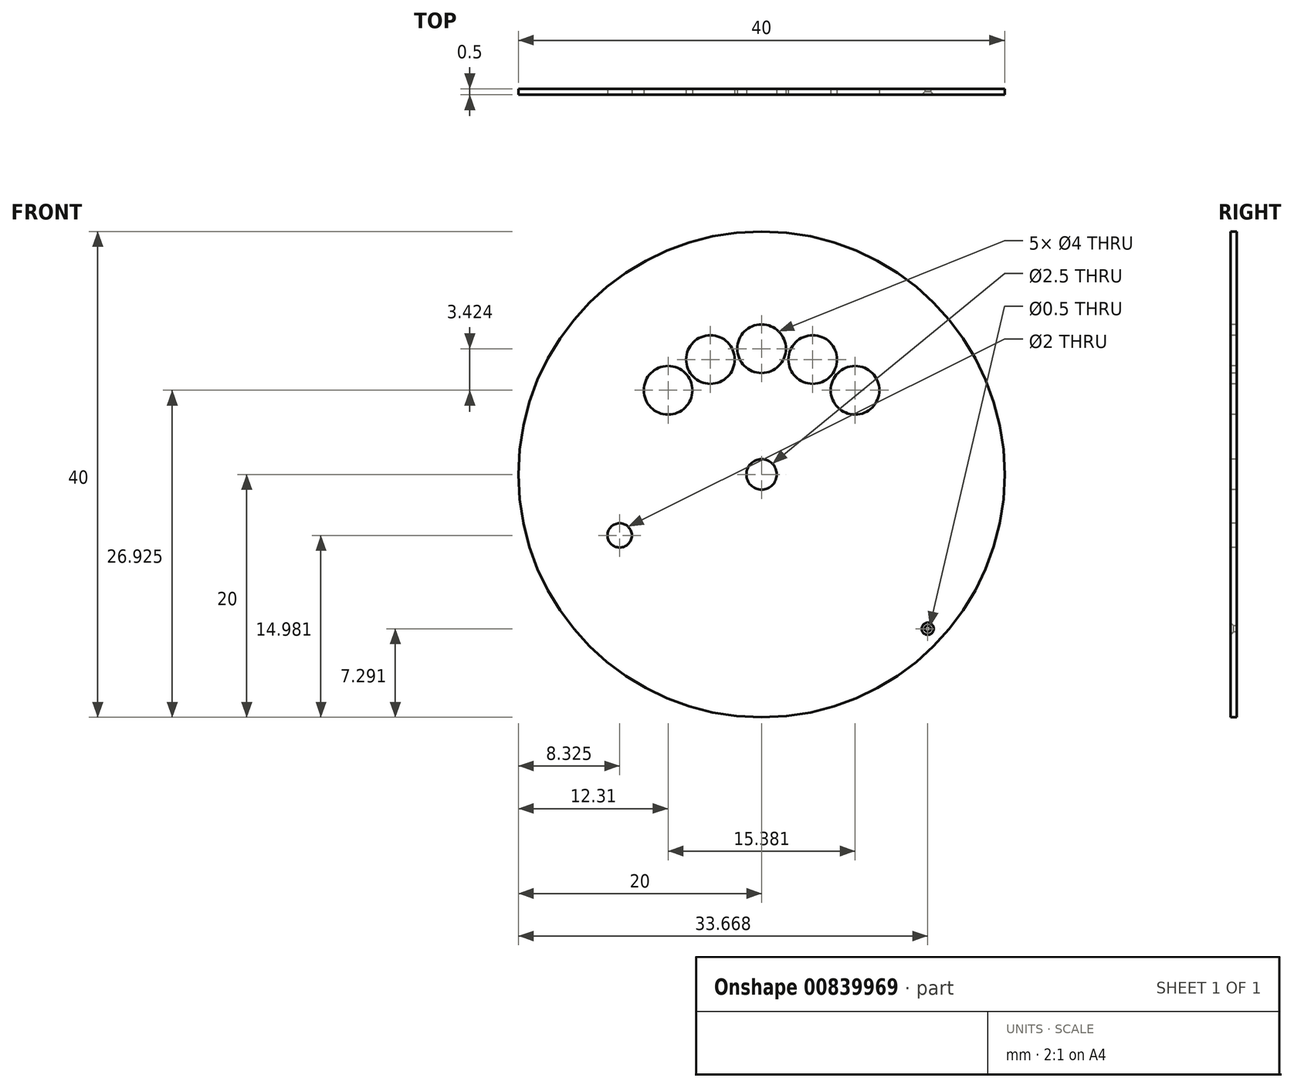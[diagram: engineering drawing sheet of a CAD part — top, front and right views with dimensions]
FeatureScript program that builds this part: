
annotation { "Feature Type Name" : "Feature", "Feature Type Description" : "" }
export const myFeature = defineFeature(function(context is Context, id is Id, definition is map)
    precondition{}
    {
        {
            var Q0;
            Q0=qCreatedBy(makeId("Front.planeOp"),FACE);
            var sketch = newSketch(context, id + "F0", { "sketchPlane" : qUnion([Q0])});
            skCircle(sketch, "E0", {"center": v(0, 0) * mm, "radius": 20 * mm});
            skSolve(sketch);
        }
        {
            var Q0;
            Q0 = qSketchRegion(id + "F0", true);
            extrude(context, id + "F1", {"entities" : qUnion([Q0]), "depth" : .5 * mm, "offsetDistance" : 25.4 * mm});
        }
        {
            var Q0;
            Q0=makeQuery(id+"F1.opExtrude","CAP_FACE",FACE,{"disambiguationData":[OSD([sQuery(id+"F0.wireOp",EDGE,"E0")])],"isStart":false});
            var sketch = newSketch(context, id + "F2", { "sketchPlane" : qUnion([Q0])});
            skPoint(sketch, "E1", {"position": v(0, 0) * mm});
            skSolve(sketch);
        }
        {
            var Q0;
            Q0=sQuery(id+"F2.wireOp",VERTEX,"E1");
            var Q1;
            Q1=makeQuery(id+"F1.opExtrude","SWEPT_BODY",BODY,{"disambiguationData":[OSD([sQuery(id+"F0.wireOp",EDGE,"E0")])]});
            hole(context, id + "F3", {"style" : HoleStyle.SIMPLE, "endStyle" : HoleEndStyle.THROUGH, "holeDiameter" : 2.5 * mm, "majorDiameter" : 6.35 * mm, "isTappedThrough" : true, "tappedDepth" : 12.7 * mm, "tapClearance" : 3, "locations" : qUnion([Q0]), "scope" : qUnion([Q1])});
        }
        {
            var Q0;
            Q0=makeQuery(id+"F1.opExtrude","CAP_FACE",FACE,{"disambiguationData":[OSD([sQuery(id+"F0.wireOp",EDGE,"E0")])],"isStart":false});
            var sketch = newSketch(context, id + "F4", { "sketchPlane" : qUnion([Q0])});
            skLineSegment(sketch, "E2", {"start": v(0, 0) * mm, "end": v(-22.97, 13.26) * mm, "construction": true});
            skLineSegment(sketch, "E3", {"start": v(-22.97, 13.26) * mm, "end": v(0, 0) * mm, "construction": true});
            skLineSegment(sketch, "E4", {"start": v(22.81, 13.17) * mm, "end": v(0, 0) * mm, "construction": true});
            skCircle(sketch, "E5", {"center": v(0, 0) * mm, "radius": 12.5 * mm, "construction": true});
            skCircle(sketch, "E6", {"center": v(-7.7, 6.92) * mm, "radius": 2.15 * mm, "construction": true});
            skCircle(sketch, "E7", {"center": v(-4.2, 9.45) * mm, "radius": 2.15 * mm, "construction": true});
            skCircle(sketch, "E8", {"center": v(0, 10.35) * mm, "radius": 2.15 * mm, "construction": true});
            skCircle(sketch, "E9", {"center": v(4.2, 9.45) * mm, "radius": 2.15 * mm, "construction": true});
            skCircle(sketch, "E10", {"center": v(7.7, 6.92) * mm, "radius": 2.15 * mm, "construction": true});
            skCircle(sketch, "E11", {"center": v(-7.7, 6.92) * mm, "radius": 2 * mm});
            skCircle(sketch, "E12", {"center": v(-4.2, 9.45) * mm, "radius": 2 * mm});
            skCircle(sketch, "E13", {"center": v(0, 10.35) * mm, "radius": 2 * mm});
            skCircle(sketch, "E14", {"center": v(4.2, 9.45) * mm, "radius": 2 * mm});
            skCircle(sketch, "E15", {"center": v(7.7, 6.92) * mm, "radius": 2 * mm});
            skSolve(sketch);
        }
        {
            var Q0;
            Q0=makeQuery(id+"F4.imprint","IMPRINT",FACE,{"disambiguationData":[TD([[makeQuery(id+"F4.imprint","IMPRINT",EDGE,{"derivedFrom":sQuery(id+"F4.wireOp",EDGE,"E11")}),1.0]])]});
            var Q1;
            Q1=makeQuery(id+"F4.imprint","IMPRINT",FACE,{"disambiguationData":[TD([[makeQuery(id+"F4.imprint","IMPRINT",EDGE,{"derivedFrom":sQuery(id+"F4.wireOp",EDGE,"E12")}),1.0]])]});
            var Q2;
            Q2=makeQuery(id+"F4.imprint","IMPRINT",FACE,{"disambiguationData":[TD([[makeQuery(id+"F4.imprint","IMPRINT",EDGE,{"derivedFrom":sQuery(id+"F4.wireOp",EDGE,"E13")}),1.0]])]});
            var Q3;
            Q3=makeQuery(id+"F4.imprint","IMPRINT",FACE,{"disambiguationData":[TD([[makeQuery(id+"F4.imprint","IMPRINT",EDGE,{"derivedFrom":sQuery(id+"F4.wireOp",EDGE,"E14")}),1.0]])]});
            var Q4;
            Q4=makeQuery(id+"F4.imprint","IMPRINT",FACE,{"disambiguationData":[TD([[makeQuery(id+"F4.imprint","IMPRINT",EDGE,{"derivedFrom":sQuery(id+"F4.wireOp",EDGE,"E15")}),1.0]])]});
            extrude(context, id + "F5", {"entities" : qUnion([Q0, Q1, Q2, Q3, Q4]), "operationType" : NewBodyOperationType.REMOVE, "oppositeDirection" : true, "depth" : 25.4 * mm, "offsetDistance" : 25.4 * mm});
        }
        {
            var Q0;
            Q0=makeQuery(id+"F1.opExtrude","CAP_FACE",FACE,{"disambiguationData":[OSD([sQuery(id+"F0.wireOp",EDGE,"E0")])],"isStart":false});
            var sketch = newSketch(context, id + "F6", { "sketchPlane" : qUnion([Q0])});
            skPoint(sketch, "E16", {"position": v(13.67, -12.7) * mm});
            skSolve(sketch);
        }
        {
            var Q0;
            Q0=sQuery(id+"F6.wireOp",VERTEX,"E16");
            var Q1;
            Q1=makeQuery(id+"F1.opExtrude","SWEPT_BODY",BODY,{"disambiguationData":[OSD([sQuery(id+"F0.wireOp",EDGE,"E0")])]});
            hole(context, id + "F7", {"style" : HoleStyle.C_SINK, "endStyle" : HoleEndStyle.THROUGH, "holeDiameter" : .5 * mm, "cSinkDiameter" : 1 * mm, "cSinkAngle" : 90 * degree, "majorDiameter" : 6.35 * mm, "isTappedThrough" : true, "tappedDepth" : 12.7 * mm, "tapClearance" : 3, "locations" : qUnion([Q0]), "scope" : qUnion([Q1])});
        }
        {
            var Q0;
            Q0=makeQuery(id+"F6.imprint","IMPRINT",FACE,{"disambiguationData":[TD([[makeQuery(id+"F6.imprint","IMPRINT",EDGE,{"derivedFrom":makeQuery(id+"F1.opExtrude","CAP_EDGE",EDGE,{"disambiguationData":[OSD([sQuery(id+"F0.wireOp",EDGE,"E0")])],"isStart":false})}),1.0]])]});
            var sketch = newSketch(context, id + "F8", { "sketchPlane" : qUnion([Q0])});
            skPoint(sketch, "E17", {"position": v(-11.68, -5.02) * mm});
            skSolve(sketch);
        }
        {
            var Q0;
            Q0=sQuery(id+"F8.wireOp",VERTEX,"E17");
            var Q1;
            Q1=makeQuery(id+"F1.opExtrude","SWEPT_BODY",BODY,{"disambiguationData":[OSD([sQuery(id+"F0.wireOp",EDGE,"E0")])]});
            hole(context, id + "F9", {"style" : HoleStyle.SIMPLE, "endStyle" : HoleEndStyle.THROUGH, "holeDiameter" : 2 * mm, "majorDiameter" : 6.35 * mm, "isTappedThrough" : true, "tappedDepth" : 12.7 * mm, "tapClearance" : 3, "locations" : qUnion([Q0]), "scope" : qUnion([Q1])});
        }
    });
